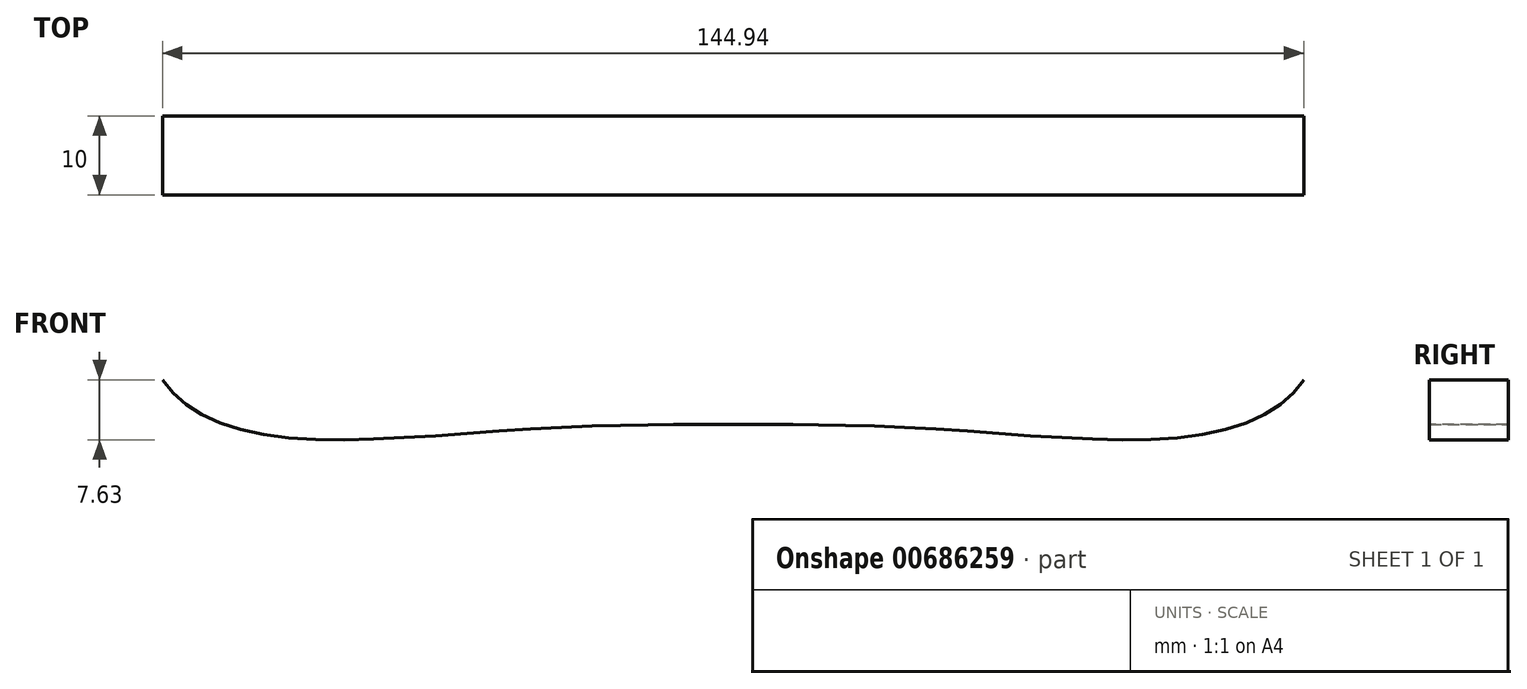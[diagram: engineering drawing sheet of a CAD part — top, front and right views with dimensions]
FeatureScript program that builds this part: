
annotation { "Feature Type Name" : "Feature", "Feature Type Description" : "" }
export const myFeature = defineFeature(function(context is Context, id is Id, definition is map)
    precondition{}
    {
        {
            var Q0;
            Q0=qCreatedBy(makeId("Front.planeOp"),FACE);
            var sketch = newSketch(context, id + "F0", { "sketchPlane" : qUnion([Q0])});
            skFitSpline(sketch, "E0", {"points": [v(-72.47, 8.5) * mm, v(-59.81, 1.57) * mm, v(-25.08, 2.28) * mm, v(0, 2.83) * mm], "startDerivative": vector(25.89, -40.68) * mm, "endDerivative": vector(44.37, 0) * mm});
            skFitSpline(sketch, "E1.MirrorCS", {"points": [v(72.47, 8.5) * mm, v(59.81, 1.57) * mm, v(25.08, 2.28) * mm, v(0, 2.83) * mm], "startDerivative": vector(-25.89, -40.68) * mm, "endDerivative": vector(-44.37, 0) * mm});
            skSolve(sketch);
        }
        {
            var Q0;
            Q0=sQuery(id+"F0.wireOp",EDGE,"E1.MirrorCS");
            var Q1;
            Q1=sQuery(id+"F0.wireOp",EDGE,"E0");
            extrude(context, id + "F1", {"bodyType" : ToolBodyType.SURFACE, "surfaceEntities" : qUnion([Q0, Q1]), "depth" : 10 * mm, "offsetDistance" : 25 * mm});
        }
    });
